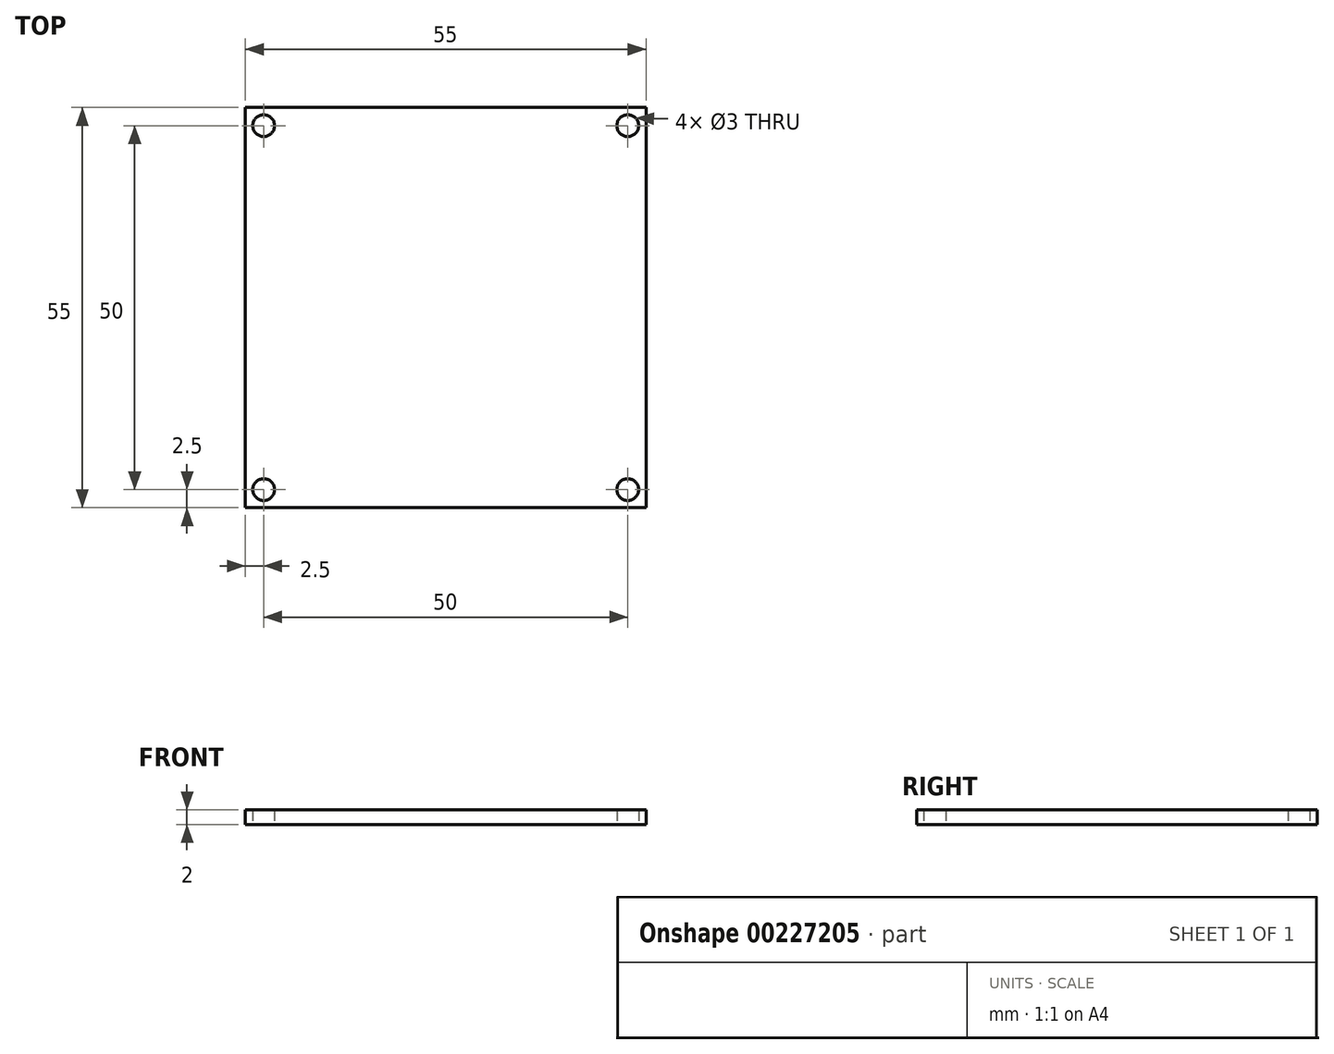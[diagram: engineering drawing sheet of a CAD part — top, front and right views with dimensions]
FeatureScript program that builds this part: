
annotation { "Feature Type Name" : "Feature", "Feature Type Description" : "" }
export const myFeature = defineFeature(function(context is Context, id is Id, definition is map)
    precondition{}
    {
        {
            var Q0;
            Q0=qCreatedBy(makeId("Top.planeOp"),FACE);
            var sketch = newSketch(context, id + "F0", { "sketchPlane" : qUnion([Q0])});
            skLineSegment(sketch, "E0.bottom", {"start": v(27.5, -27.5) * mm, "end": v(-27.5, -27.5) * mm});
            skLineSegment(sketch, "E0.top", {"start": v(27.5, 27.5) * mm, "end": v(-27.5, 27.5) * mm});
            skLineSegment(sketch, "E0.left", {"start": v(27.5, -27.5) * mm, "end": v(27.5, 27.5) * mm});
            skLineSegment(sketch, "E0.right", {"start": v(-27.5, -27.5) * mm, "end": v(-27.5, 27.5) * mm});
            skPoint(sketch, "E0.middle", {"position": v(0, 0) * mm});
            skLineSegment(sketch, "E1.bottom", {"start": v(25, -25) * mm, "end": v(-25, -25) * mm, "construction": true});
            skLineSegment(sketch, "E1.top", {"start": v(25, 25) * mm, "end": v(-25, 25) * mm, "construction": true});
            skLineSegment(sketch, "E1.left", {"start": v(25, -25) * mm, "end": v(25, 25) * mm, "construction": true});
            skLineSegment(sketch, "E1.right", {"start": v(-25, -25) * mm, "end": v(-25, 25) * mm, "construction": true});
            skCircle(sketch, "E2", {"center": v(-25, 25) * mm, "radius": 1.5 * mm});
            skCircle(sketch, "E3.1.0", {"center": v(-25, -25) * mm, "radius": 1.5 * mm});
            skCircle(sketch, "E3.2.0", {"center": v(25, -25) * mm, "radius": 1.5 * mm});
            skCircle(sketch, "E3.3.0", {"center": v(25, 25) * mm, "radius": 1.5 * mm});
            skSolve(sketch);
        }
        {
            var Q0;
            Q0 = qSketchRegion(id + "F0", true);
            extrude(context, id + "F1", {"entities" : qUnion([Q0]), "depth" : 2 * mm});
        }
    });
